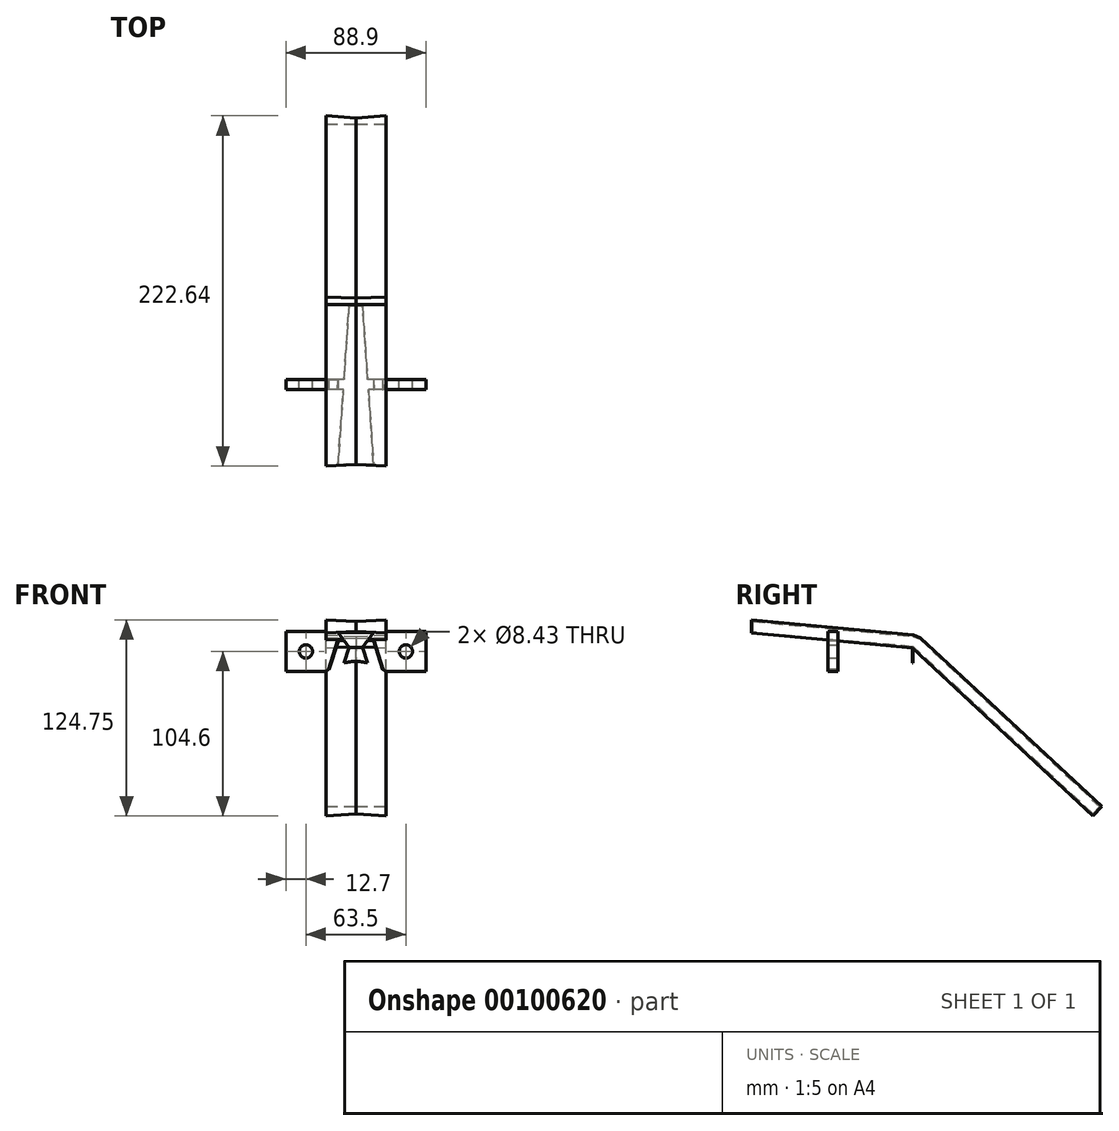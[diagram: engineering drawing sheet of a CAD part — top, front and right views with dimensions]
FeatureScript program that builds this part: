
annotation { "Feature Type Name" : "Feature", "Feature Type Description" : "" }
export const myFeature = defineFeature(function(context is Context, id is Id, definition is map)
    precondition{}
    {
        {
            var Q0;
            Q0=qCreatedBy(makeId("Front.planeOp"),FACE);
            var sketch = newSketch(context, id + "F0", { "sketchPlane" : qUnion([Q0])});
            skArc(sketch, "E0", {"start": v(-19.05, 25.4) * mm, "mid": v(0, -31.75) * mm, "end": v(19.05, 25.4) * mm});
            skLineSegment(sketch, "E1", {"start": v(-11.11, 50.8) * mm, "end": v(11.11, 50.8) * mm});
            skPoint(sketch, "E2.orphan", {"position": v(-31.75, 0) * mm});
            skPoint(sketch, "E3.orphan", {"position": v(31.75, 0) * mm});
            skLineSegment(sketch, "E4", {"start": v(-19.05, 25.4) * mm, "end": v(-11.11, 50.8) * mm});
            skLineSegment(sketch, "E5", {"start": v(11.11, 50.8) * mm, "end": v(19.05, 25.4) * mm});
            skSolve(sketch);
        }
        {
            var Q0;
            Q0=qCreatedBy(makeId("Front.planeOp"),FACE);
            cPlane(context, id + "F1", {"entities" : qUnion([Q0]), "cplaneType" : CPlaneType.OFFSET, "offset" : 101.6 * mm, "oppositeDirection" : true, "width" : 152.4 * mm, "height" : 152.4 * mm});
        }
        {
            var Q0;
            Q0=qCreatedBy(id+"F1.planeOp",FACE);
            var sketch = newSketch(context, id + "F2", { "sketchPlane" : qUnion([Q0])});
            skArc(sketch, "E6", {"start": v(-19.05, 25.4) * mm, "mid": v(0, -31.75) * mm, "end": v(19.05, 25.4) * mm});
            skLineSegment(sketch, "E7", {"start": v(-11.11, 50.8) * mm, "end": v(11.11, 50.8) * mm});
            skPoint(sketch, "E8.orphan", {"position": v(-31.75, 0) * mm});
            skPoint(sketch, "E9.orphan", {"position": v(31.75, 0) * mm});
            skLineSegment(sketch, "E10", {"start": v(-19.05, 25.4) * mm, "end": v(-11.11, 50.8) * mm});
            skLineSegment(sketch, "E11", {"start": v(11.11, 50.8) * mm, "end": v(19.05, 25.4) * mm});
            skArc(sketch, "E12.0", {"start": v(-10.97, 19.33) * mm, "mid": v(0, -22.23) * mm, "end": v(10.97, 19.33) * mm});
            skLineSegment(sketch, "E12.1", {"start": v(-10.97, 19.33) * mm, "end": v(-4.1, 41.28) * mm});
            skLineSegment(sketch, "E12.2", {"start": v(-4.1, 41.28) * mm, "end": v(4.1, 41.28) * mm});
            skLineSegment(sketch, "E12.3", {"start": v(4.1, 41.28) * mm, "end": v(10.97, 19.33) * mm});
            skSolve(sketch);
        }
        {
            var Q0;
            Q0=makeQuery(id+"F2.imprint","IMPRINT",FACE,{"disambiguationData":[TD([[makeQuery(id+"F2.imprint","IMPRINT",EDGE,{"derivedFrom":sQuery(id+"F2.wireOp",EDGE,"E12.0")}),1.0]])]});
            var Q1;
            Q1=makeQuery(id+"F0.imprint","IMPRINT",FACE,{"disambiguationData":[TD([[makeQuery(id+"F0.imprint","IMPRINT",EDGE,{"derivedFrom":sQuery(id+"F0.wireOp",EDGE,"E0")}),1.0]])]});
            loft(context, id + "F3", {"sheetProfilesArray" : [{ "sheetProfileEntities" : qUnion([Q0]) }, { "sheetProfileEntities" : qUnion([Q1]) }]});
        }
        {
            var Q0;
            Q0=qCreatedBy(makeId("Right.planeOp"),FACE);
            var sketch = newSketch(context, id + "F4", { "sketchPlane" : qUnion([Q0])});
            skLineSegment(sketch, "E13", {"start": v(101.6, 41.28) * mm, "end": v(0, 50.8) * mm});
            skLineSegment(sketch, "E14", {"start": v(0, 50.8) * mm, "end": v(0, 57.15) * mm});
            skLineSegment(sketch, "E15", {"start": v(101.6, 47.62) * mm, "end": v(0, 57.15) * mm});
            skLineSegment(sketch, "E16", {"start": v(101.6, 41.28) * mm, "end": v(178.71, -30.48) * mm});
            skLineSegment(sketch, "E17", {"start": v(101.6, 47.63) * mm, "end": v(105.93, 45.92) * mm});
            skLineSegment(sketch, "E18", {"start": v(105.93, 45.92) * mm, "end": v(183.04, -25.83) * mm});
            skLineSegment(sketch, "E19", {"start": v(178.71, -30.48) * mm, "end": v(215.9, -65.09) * mm});
            skLineSegment(sketch, "E20", {"start": v(183.04, -25.83) * mm, "end": v(220.23, -60.44) * mm});
            skLineSegment(sketch, "E21", {"start": v(215.9, -65.09) * mm, "end": v(220.23, -60.44) * mm});
            skSolve(sketch);
        }
        {
            var Q0;
            Q0 = qSketchRegion(id + "F4", true);
            extrude(context, id + "F5", {"entities" : qUnion([Q0]), "operationType" : NewBodyOperationType.ADD, "endBound" : BoundingType.SYMMETRIC, "depth" : 38.1 * mm, "hasDraft" : true, "draftAngle" : 3 * degree});
        }
        {
            var Q0;
            Q0=qCreatedBy(makeId("Top.planeOp"),FACE);
            var sketch = newSketch(context, id + "F6", { "sketchPlane" : qUnion([Q0])});
            skLineSegment(sketch, "E22.bottom", {"start": v(44.45, 53.98) * mm, "end": v(-44.45, 53.98) * mm});
            skLineSegment(sketch, "E22.top", {"start": v(44.45, 47.63) * mm, "end": v(-44.45, 47.62) * mm});
            skLineSegment(sketch, "E22.left", {"start": v(44.45, 53.98) * mm, "end": v(44.45, 47.63) * mm});
            skLineSegment(sketch, "E22.right", {"start": v(-44.45, 53.98) * mm, "end": v(-44.45, 47.62) * mm});
            skPoint(sketch, "E22.middle", {"position": v(0, 50.8) * mm});
            skSolve(sketch);
        }
        {
            var Q0;
            Q0 = qSketchRegion(id + "F6", true);
            extrude(context, id + "F7", {"entities" : qUnion([Q0]), "operationType" : NewBodyOperationType.ADD, "depth" : 50.8 * mm, "hasSecondDirection" : true, "secondDirectionOppositeDirection" : false, "secondDirectionDepth" : 25.4 * mm});
        }
        {
            var Q0;
            {var subQ1=sQuery(id+"F6.wireOp",EDGE,"E22.left");var subQ3=sQuery(id+"F6.wireOp",EDGE,"E22.bottom");Q0=makeQuery(id+"F7.boolean.opBoolean","SPLIT",FACE,{"disambiguationData":[TD([makeQuery(id+"F7.opExtrude","SWEPT_FACE",FACE,{"disambiguationData":[OSD([subQ1])]})])],"derivedFrom":makeQuery(id+"F7.opExtrude","SWEPT_FACE",FACE,{"disambiguationData":[OSD([subQ3])]})});}
            var sketch = newSketch(context, id + "F8", { "sketchPlane" : qUnion([Q0])});
            skPoint(sketch, "E23", {"position": v(-31.75, 38.1) * mm});
            skPoint(sketch, "E24.MirrorP", {"position": v(31.75, 38.1) * mm});
            skSolve(sketch);
        }
        {
            var Q0;
            Q0=sQuery(id+"F8.wireOp",VERTEX,"E23");
            var Q1;
            Q1=sQuery(id+"F8.wireOp",VERTEX,"E24.MirrorP");
            var Q2;
            Q2=makeQuery(id+"FfEzCMeOqPjsGG8_1.splitOp","SPLIT",BODY,{"derivedFrom":makeQuery(id+"F3.opLoft","SWEPT_BODY",BODY,{"disambiguationData":[OSD([makeQuery(id+"F0.imprint","IMPRINT",FACE,{"disambiguationData":[TD([[makeQuery(id+"F0.imprint","IMPRINT",EDGE,{"derivedFrom":sQuery(id+"F0.wireOp",EDGE,"E0")}),1.0]])]}),makeQuery(id+"F2.imprint","IMPRINT",FACE,{"disambiguationData":[TD([[makeQuery(id+"F2.imprint","IMPRINT",EDGE,{"derivedFrom":sQuery(id+"F2.wireOp",EDGE,"E12.0")}),1.0]])]})])]})});
            hole(context, id + "F9", {"style" : HoleStyle.SIMPLE, "endStyle" : HoleEndStyle.THROUGH, "standardTappedOrClearance" : lookupTablePath({ "standard" : "ANSI", "fit" : "Normal (ASME)", "size" : "5/16", "type" : "Clearance" }), "standardBlindInLast" : lookupTablePath({ "fit" : "Free", "standard" : "ANSI", "size" : "5/16", "type" : "Clearance" }), "holeDiameter" : 8.43 * mm, "locations" : qUnion([Q0, Q1]), "scope" : qUnion([Q2]), "isTappedThrough" : true});
        }
        {
            var Q0;
            Q0=makeQuery(id+"F3.opLoft","CAP_FACE",FACE,{"disambiguationData":[OSD([makeQuery(id+"F0.imprint","IMPRINT",FACE,{"disambiguationData":[TD([[makeQuery(id+"F0.imprint","IMPRINT",EDGE,{"derivedFrom":sQuery(id+"F0.wireOp",EDGE,"E0")}),1.0]])]})])],"isStart":true});
            var sketch = newSketch(context, id + "F10", { "sketchPlane" : qUnion([Q0])});
            skCircle(sketch, "E25", {"center": v(0, 0) * mm, "radius": 31.75 * mm});
            skSolve(sketch);
        }
        {
            var Q0;
            {var subQ0=sQuery(id+"F10.wireOp",EDGE,"E25");var subQ1=sQuery(id+"F0.wireOp",EDGE,"E1");var subQ2=sQuery(id+"F0.wireOp",EDGE,"E0");var subQ3=makeQuery(id+"F10.imprint","INTERSECT",VERTEX,{"derivedFrom":[makeQuery(id+"F3.opLoft","MID_CAP_EDGE",EDGE,{"disambiguationData":[OSD([subQ2,subQ1,sQuery(id+"F0.wireOp",EDGE,"E4")])],"capPos":1.0}),subQ0]});Q0=makeQuery(id+"F10.imprint","IMPRINT",FACE,{"disambiguationData":[TD([[makeQuery(id+"F10.imprint","IMPRINT",EDGE,{"disambiguationData":[TD([[subQ3,-1.0]])],"derivedFrom":subQ0}),1.0]])]});}
            extrude(context, id + "F11", {"entities" : qUnion([Q0]), "operationType" : NewBodyOperationType.REMOVE, "oppositeDirection" : true, "depth" : 106.12 * mm});
        }
        {
            var Q0;
            Q0=makeQuery(id+"F3.opLoft","CAP_FACE",FACE,{"disambiguationData":[OSD([makeQuery(id+"F0.imprint","IMPRINT",FACE,{"disambiguationData":[TD([[makeQuery(id+"F0.imprint","IMPRINT",EDGE,{"derivedFrom":sQuery(id+"F0.wireOp",EDGE,"E0")}),1.0]])]})])],"isStart":true});
            var sketch = newSketch(context, id + "F12", { "sketchPlane" : qUnion([Q0])});
            skLineSegment(sketch, "E26.bottom", {"start": v(-19.05, 25.4) * mm, "end": v(19.05, 25.4) * mm});
            skLineSegment(sketch, "E26.top", {"start": v(-19.05, 50.2) * mm, "end": v(19.05, 50.2) * mm});
            skLineSegment(sketch, "E26.left", {"start": v(-19.05, 25.4) * mm, "end": v(-19.05, 50.2) * mm});
            skLineSegment(sketch, "E26.right", {"start": v(19.05, 25.4) * mm, "end": v(19.05, 50.2) * mm});
            skSolve(sketch);
        }
        {
            var Q0;
            Q0=makeQuery(id+"F5.opExtrude","CAP_FACE",FACE,{"disambiguationData":[OSD([sQuery(id+"F4.wireOp",EDGE,"E13"),sQuery(id+"F4.wireOp",EDGE,"E14"),sQuery(id+"F4.wireOp",EDGE,"E15"),sQuery(id+"F4.wireOp",EDGE,"E16"),sQuery(id+"F4.wireOp",EDGE,"E17"),sQuery(id+"F4.wireOp",EDGE,"E18"),sQuery(id+"F4.wireOp",EDGE,"E19"),sQuery(id+"F4.wireOp",EDGE,"E20"),sQuery(id+"F4.wireOp",EDGE,"E21")])],"isStart":true});
            var sketch = newSketch(context, id + "F13", { "sketchPlane" : qUnion([Q0])});
            skLineSegment(sketch, "E27", {"start": v(1, 49.9) * mm, "end": v(-101.17, 40.31) * mm});
            skSolve(sketch);
        }
        {
            var Q0;
            {var subQ2=sQuery(id+"F0.wireOp",EDGE,"E0");var subQ3=sQuery(id+"F0.wireOp",EDGE,"E1");var subQ4=sQuery(id+"F0.wireOp",EDGE,"E4");var subQ7=makeQuery(id+"F3.opLoft","MID_CAP_EDGE",EDGE,{"disambiguationData":[OSD([subQ2,subQ3,subQ4])],"capPos":1.0});Q0=makeQuery(id+"F12.imprint","IMPRINT",FACE,{"disambiguationData":[TD([[makeQuery(id+"F12.imprint","IMPRINT",EDGE,{"derivedFrom":subQ7}),1.0]])]});}
            var Q1;
            Q1=sQuery(id+"F13.wireOp",EDGE,"E27");
            sweep(context, id + "F14", {"operationType" : NewBodyOperationType.REMOVE, "profiles" : qUnion([Q0]), "path" : qUnion([Q1])});
        }
        {
            var Q0;
            Q0=makeQuery(id+"F14.boolean.opBoolean","COPY",FACE,{"disambiguationData":[OD(1.0)],"derivedFrom":makeQuery(id+"F14.opSweep","SWEPT_FACE",FACE,{"disambiguationData":[OSD([sQuery(id+"F0.wireOp",EDGE,"E0"),sQuery(id+"F0.wireOp",EDGE,"E1"),sQuery(id+"F0.wireOp",EDGE,"E4"),sQuery(id+"F13.wireOp",EDGE,"E27")])]})});
            var sketch = newSketch(context, id + "F15", { "sketchPlane" : qUnion([Q0])});
            skLineSegment(sketch, "E28.bottom", {"start": v(46.92, 20.28) * mm, "end": v(53.28, 20.28) * mm});
            skLineSegment(sketch, "E28.top", {"start": v(46.92, 39.72) * mm, "end": v(53.28, 39.72) * mm});
            skLineSegment(sketch, "E28.left", {"start": v(46.92, 20.28) * mm, "end": v(46.92, 39.72) * mm});
            skLineSegment(sketch, "E28.right", {"start": v(53.28, 20.28) * mm, "end": v(53.28, 39.72) * mm});
            skSolve(sketch);
        }
        {
            var Q0;
            Q0 = qSketchRegion(id + "F15", true);
            extrude(context, id + "F16", {"entities" : qUnion([Q0]), "operationType" : NewBodyOperationType.ADD, "depth" : 0.19 * mm});
        }
        {
            var Q0;
            Q0=makeQuery(id+"F14.boolean.opBoolean","COPY",FACE,{"disambiguationData":[OD(1.0)],"derivedFrom":makeQuery(id+"F14.opSweep","SWEPT_FACE",FACE,{"disambiguationData":[OSD([sQuery(id+"F0.wireOp",EDGE,"E0"),sQuery(id+"F0.wireOp",EDGE,"E1"),sQuery(id+"F0.wireOp",EDGE,"E5"),sQuery(id+"F13.wireOp",EDGE,"E27")])]})});
            var sketch = newSketch(context, id + "F17", { "sketchPlane" : qUnion([Q0])});
            skLineSegment(sketch, "E29.bottom", {"start": v(-53.28, 39.72) * mm, "end": v(-46.92, 39.72) * mm});
            skLineSegment(sketch, "E29.top", {"start": v(-53.28, 20.28) * mm, "end": v(-46.92, 20.28) * mm});
            skLineSegment(sketch, "E29.left", {"start": v(-53.28, 39.72) * mm, "end": v(-53.28, 20.28) * mm});
            skLineSegment(sketch, "E29.right", {"start": v(-46.92, 39.72) * mm, "end": v(-46.92, 20.28) * mm});
            skSolve(sketch);
        }
        {
            var Q0;
            {var subQ0=sQuery(id+"F17.wireOp",EDGE,"E29.bottom");Q0=makeQuery(id+"F17.imprint","IMPRINT",FACE,{"disambiguationData":[TD([[makeQuery(id+"F17.imprint","IMPRINT",EDGE,{"derivedFrom":subQ0}),-1.0]])]});}
            extrude(context, id + "F18", {"entities" : qUnion([Q0]), "operationType" : NewBodyOperationType.ADD, "depth" : 0.19 * mm});
        }
    });
